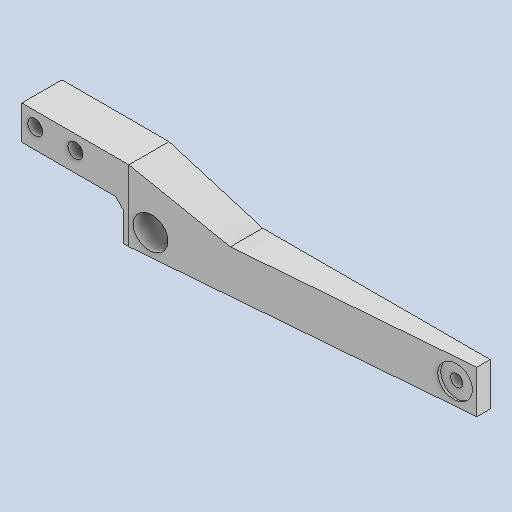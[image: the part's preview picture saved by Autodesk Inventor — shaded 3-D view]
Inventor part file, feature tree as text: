
AUTODESK INVENTOR PART (.ipt)
format: ipt  version: 2023 (Build 270158000, 158)  size: 128,000 bytes
history: native  units: in
note: dims shown in document units (in); Inventor stores cm internally (conversion verified against a paired STEP export)
features: sketch x8, other x3
ambient origin geometry x8: Origin, YZ Plane, XZ Plane, XY Plane, X Axis, Y Axis, Z Axis, Center Point
bodies: Solid1 (feature_tree)
feature tree (11):
  other  "Fan_side_mount.ipt"
  other  "Solid1::Fan_side_mount.ipt"
  other  "TaggingFeature1"
  sketch  "Sketch1"  dims[d0=0.3937in]
  sketch  "Sketch2"
  sketch  "Sketch3"
  sketch  "Sketch4"
  sketch  "Sketch5"
  sketch  "Sketch6"
  sketch  "Sketch7"
  sketch  "Sketch9"
